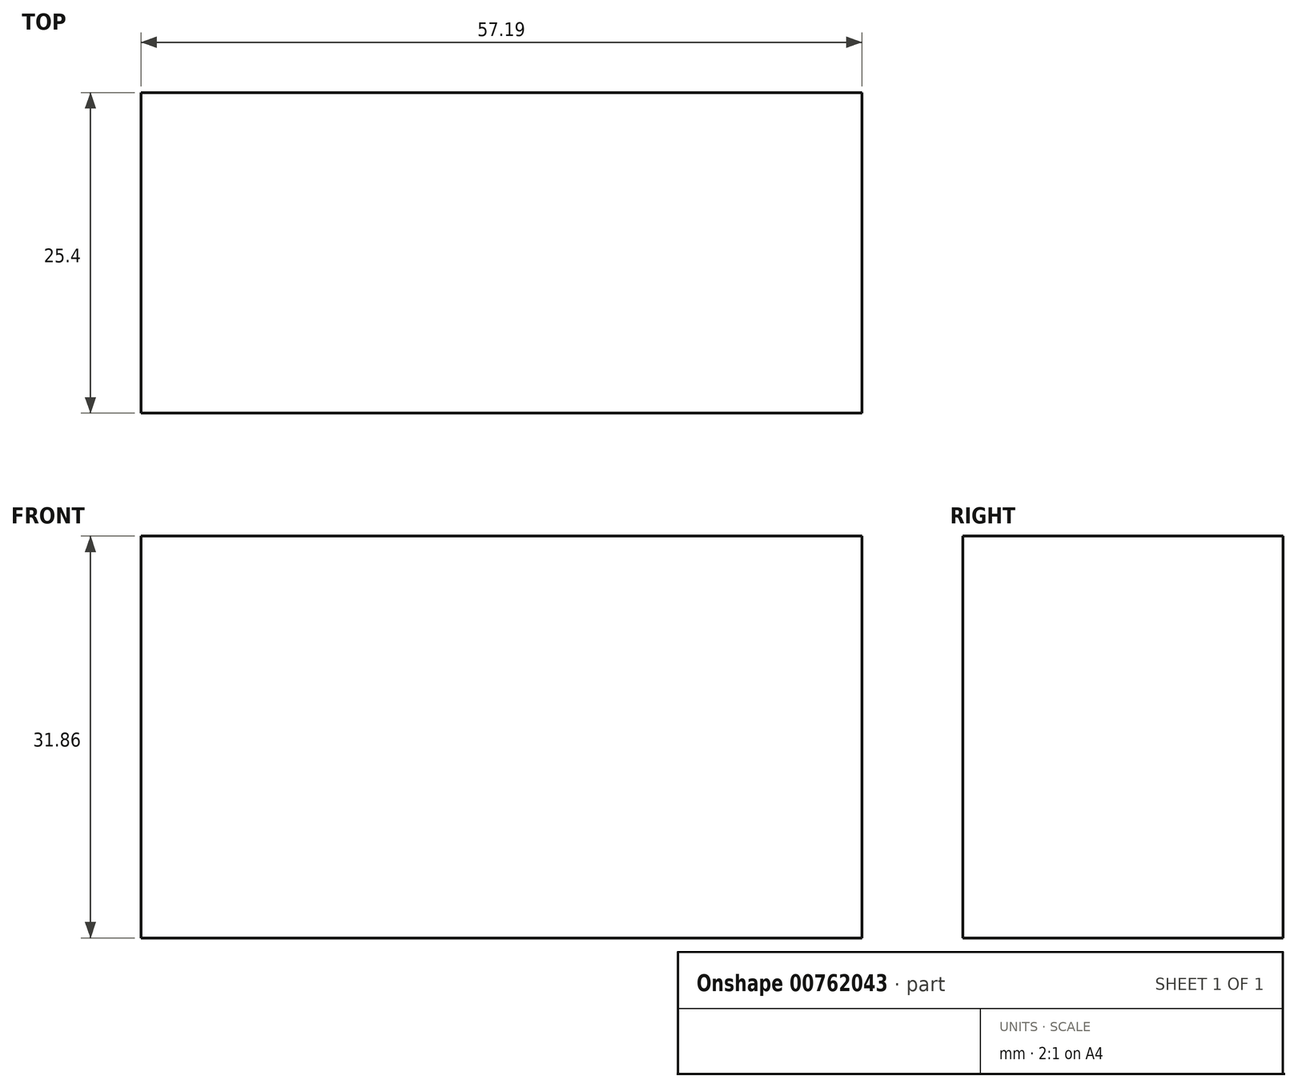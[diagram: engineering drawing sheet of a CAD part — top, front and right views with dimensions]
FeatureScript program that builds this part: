
annotation { "Feature Type Name" : "Feature", "Feature Type Description" : "" }
export const myFeature = defineFeature(function(context is Context, id is Id, definition is map)
    precondition{}
    {
        {
            var Q0;
            Q0=qCreatedBy(makeId("Front.planeOp"),FACE);
            var sketch = newSketch(context, id + "F0", { "sketchPlane" : qUnion([Q0])});
            skLineSegment(sketch, "E0", {"start": v(0, 0) * mm, "end": v(57.2, 0) * mm});
            skLineSegment(sketch, "E1", {"start": v(0, 0) * mm, "end": v(0, 31.86) * mm});
            skLineSegment(sketch, "E2", {"start": v(0, 31.86) * mm, "end": v(57.2, 31.86) * mm});
            skLineSegment(sketch, "E3", {"start": v(57.2, 31.86) * mm, "end": v(57.2, 0) * mm});
            skSolve(sketch);
        }
        {
            var Q0;
            Q0 = qSketchRegion(id + "F0", true);
            extrude(context, id + "F1", {"entities" : qUnion([Q0]), "depth" : 25.4 * mm, "offsetDistance" : 25.4 * mm});
        }
    });
